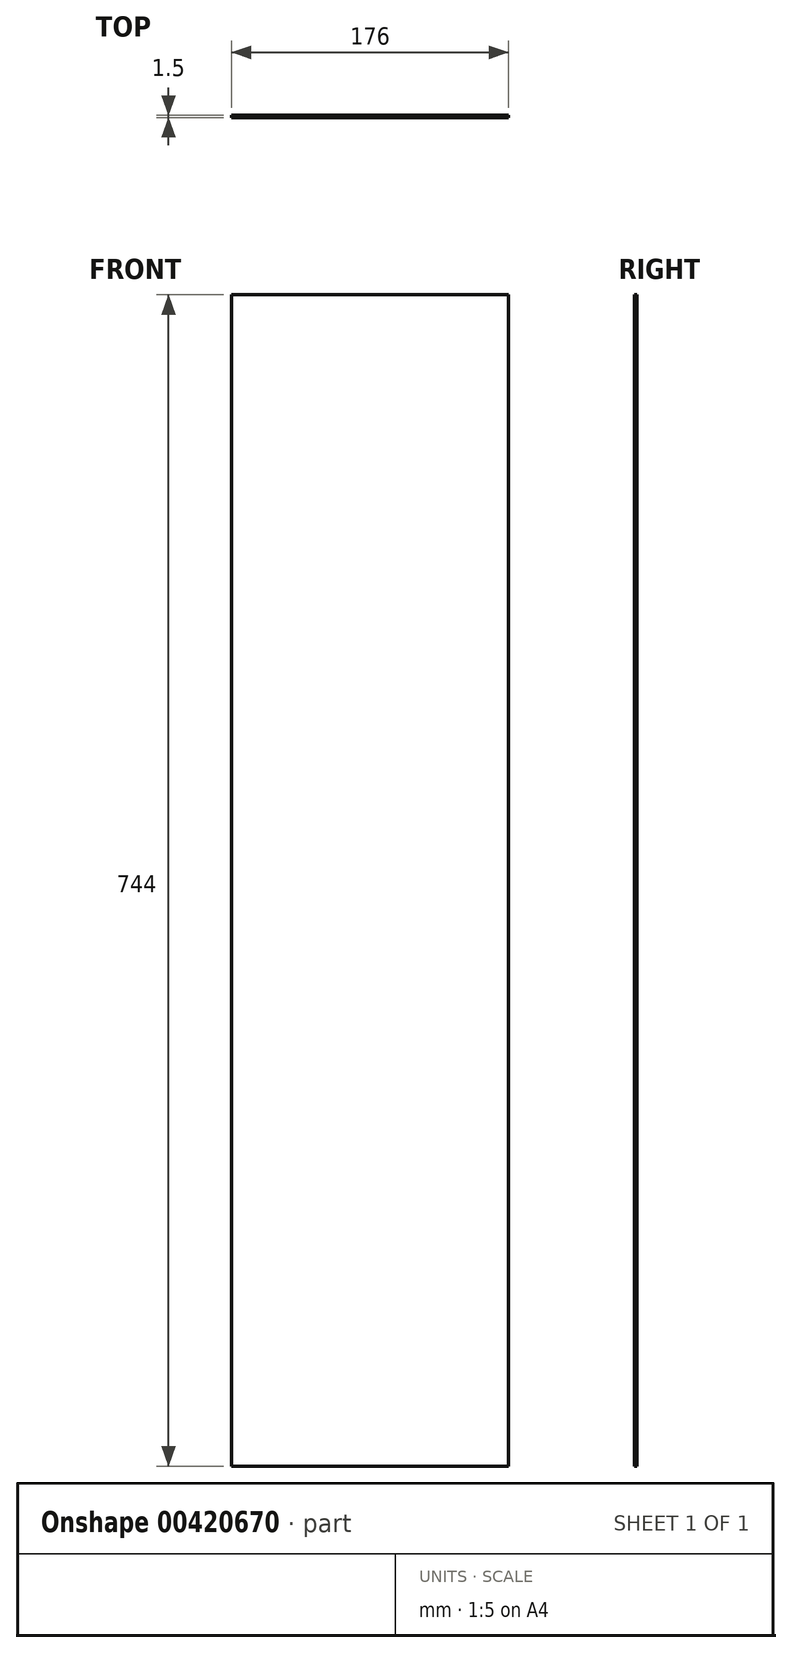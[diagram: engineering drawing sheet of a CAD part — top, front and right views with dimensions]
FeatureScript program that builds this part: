
annotation { "Feature Type Name" : "Feature", "Feature Type Description" : "" }
export const myFeature = defineFeature(function(context is Context, id is Id, definition is map)
    precondition{}
    {
        {
            var Q0;
            Q0=qCreatedBy(makeId("Front.planeOp"),FACE);
            var sketch = newSketch(context, id + "F0", { "sketchPlane" : qUnion([Q0])});
            skLineSegment(sketch, "E0.bottom", {"start": v(88, -372) * mm, "end": v(-88, -372) * mm});
            skLineSegment(sketch, "E0.top", {"start": v(88, 372) * mm, "end": v(-88, 372) * mm});
            skLineSegment(sketch, "E0.left", {"start": v(88, -372) * mm, "end": v(88, 372) * mm});
            skLineSegment(sketch, "E0.right", {"start": v(-88, -372) * mm, "end": v(-88, 372) * mm});
            skPoint(sketch, "E0.middle", {"position": v(0, 0) * mm});
            skSolve(sketch);
        }
        {
            var Q0;
            Q0=qSketchRegion(id+"F0",true);
            extrude(context, id + "F1", {"entities" : qUnion([Q0]), "depth" : 1.5 * mm});
        }
    });
